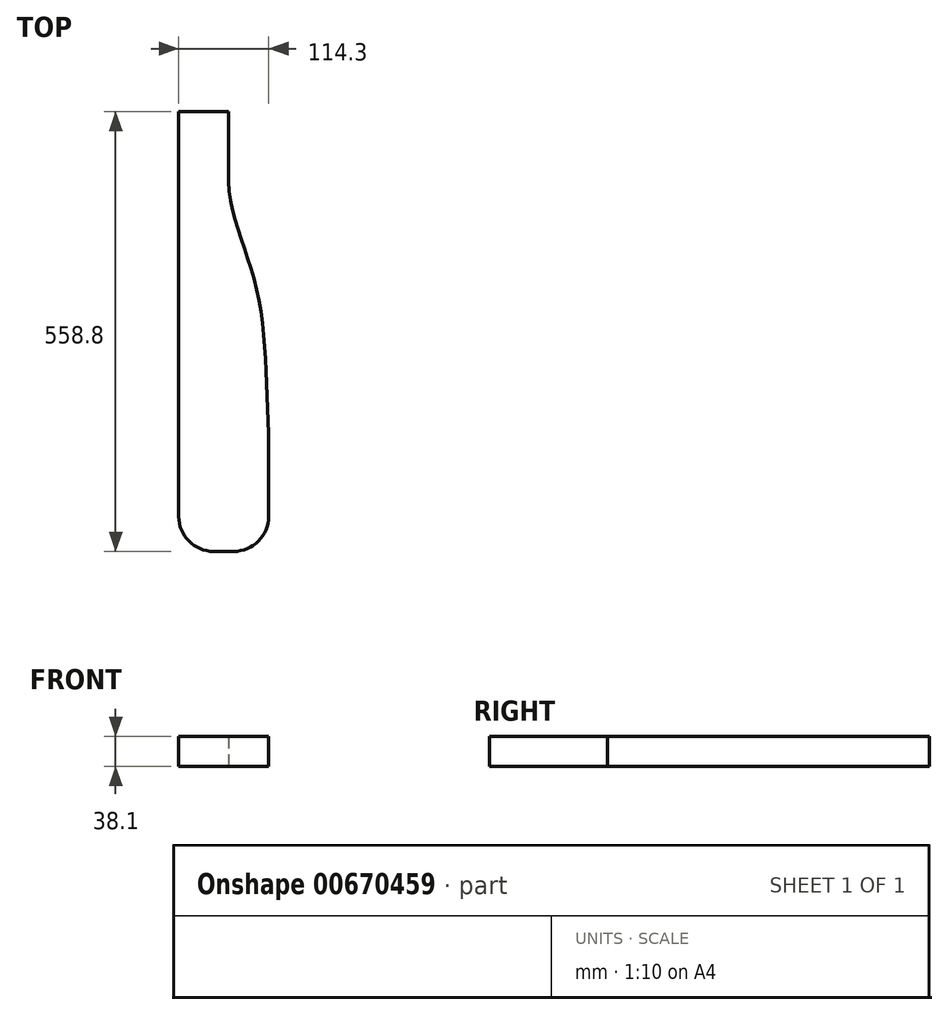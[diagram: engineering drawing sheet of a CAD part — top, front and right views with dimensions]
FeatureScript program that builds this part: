
annotation { "Feature Type Name" : "Feature", "Feature Type Description" : "" }
export const myFeature = defineFeature(function(context is Context, id is Id, definition is map)
    precondition{}
    {
        {
            var Q0;
            Q0=qCreatedBy(makeId("Top.planeOp"),FACE);
            var sketch = newSketch(context, id + "F0", { "sketchPlane" : qUnion([Q0])});
            skLineSegment(sketch, "E0.top", {"start": v(44.45, -558.8) * mm, "end": v(69.85, -558.8) * mm});
            skLineSegment(sketch, "E0.left", {"start": v(0, 0) * mm, "end": v(0, -514.35) * mm});
            skLineSegment(sketch, "E0.right", {"start": v(114.3, -408.91) * mm, "end": v(114.3, -514.35) * mm});
            skPoint(sketch, "E1.visualSharp", {"position": v(0, -558.8) * mm});
            skArc(sketch, "E1.filletArc", {"start": v(0, -514.35) * mm, "mid": v(13.02, -545.78) * mm, "end": v(44.45, -558.8) * mm});
            skPoint(sketch, "E2.visualSharp", {"position": v(114.3, -558.8) * mm});
            skArc(sketch, "E2.filletArc", {"start": v(69.85, -558.8) * mm, "mid": v(101.28, -545.78) * mm, "end": v(114.3, -514.35) * mm});
            skPoint(sketch, "E3.orphan", {"position": v(114.3, -3.5) * mm});
            skPoint(sketch, "E4.orphan", {"position": v(0, 0) * mm});
            skLineSegment(sketch, "E5", {"start": v(0, 0) * mm, "end": v(63.5, 0) * mm});
            skLineSegment(sketch, "E6", {"start": v(63.5, 0) * mm, "end": v(63.5, -88.9) * mm});
            skFitSpline(sketch, "E7", {"points": [v(63.5, -88.9) * mm, v(97.57, -219.27) * mm, v(114.3, -408.91) * mm], "startDerivative": vector(0, -283.65) * mm, "endDerivative": vector(18.93, -366.52) * mm});
            skSolve(sketch);
        }
        {
            var Q0;
            Q0=makeQuery(id+"F0.imprint","IMPRINT",FACE,{"disambiguationData":[TD([[makeQuery(id+"F0.imprint","IMPRINT",EDGE,{"derivedFrom":sQuery(id+"F0.wireOp",EDGE,"E0.left")}),1.0]])]});
            extrude(context, id + "F1", {"entities" : qUnion([Q0]), "depth" : 38.1 * mm, "offsetDistance" : 25.4 * mm});
        }
    });
